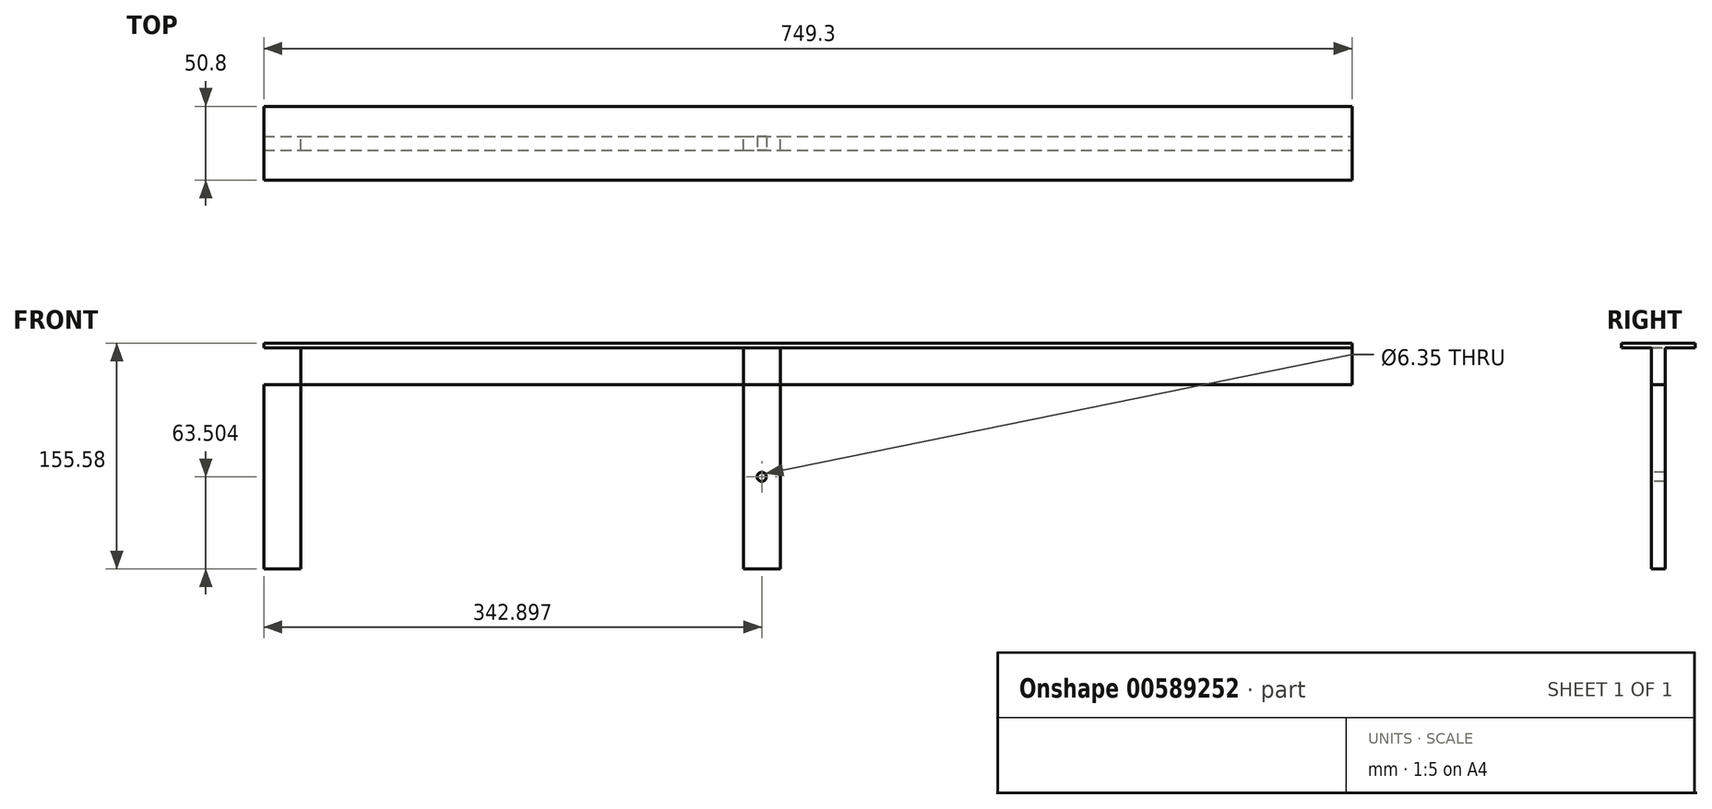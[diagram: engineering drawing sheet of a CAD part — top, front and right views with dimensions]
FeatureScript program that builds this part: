
annotation { "Feature Type Name" : "Feature", "Feature Type Description" : "" }
export const myFeature = defineFeature(function(context is Context, id is Id, definition is map)
    precondition{}
    {
        {
            var Q0;
            Q0=qCreatedBy(makeId("Front.planeOp"),FACE);
            var sketch = newSketch(context, id + "F0", { "sketchPlane" : qUnion([Q0])});
            skLineSegment(sketch, "E0.bottom", {"start": v(-685.15, -7.83) * mm, "end": v(64.15, -7.83) * mm});
            skLineSegment(sketch, "E0.top", {"start": v(-685.15, -33.23) * mm, "end": v(64.15, -33.23) * mm});
            skLineSegment(sketch, "E0.left", {"start": v(-685.15, -7.83) * mm, "end": v(-685.15, -33.23) * mm});
            skLineSegment(sketch, "E0.right", {"start": v(64.15, -7.83) * mm, "end": v(64.15, -33.23) * mm});
            skLineSegment(sketch, "E1.bottom", {"start": v(-685.15, -7.83) * mm, "end": v(-659.75, -7.83) * mm});
            skLineSegment(sketch, "E1.top", {"start": v(-685.15, -160.23) * mm, "end": v(-659.75, -160.23) * mm});
            skLineSegment(sketch, "E1.left", {"start": v(-685.15, -7.83) * mm, "end": v(-685.15, -160.23) * mm});
            skLineSegment(sketch, "E1.right", {"start": v(-659.75, -7.83) * mm, "end": v(-659.75, -160.23) * mm});
            skLineSegment(sketch, "E2.bottom", {"start": v(-354.95, -7.83) * mm, "end": v(-329.55, -7.83) * mm});
            skLineSegment(sketch, "E2.top", {"start": v(-354.95, -160.23) * mm, "end": v(-329.55, -160.23) * mm});
            skLineSegment(sketch, "E2.left", {"start": v(-354.95, -7.83) * mm, "end": v(-354.95, -160.23) * mm});
            skLineSegment(sketch, "E2.right", {"start": v(-329.55, -7.83) * mm, "end": v(-329.55, -160.23) * mm});
            skSolve(sketch);
        }
        {
            var Q0;
            {var subQ0=sQuery(id+"F0.wireOp",EDGE,"E0.right");Q0=makeQuery(id+"F0.imprint","IMPRINT",FACE,{"disambiguationData":[TD([[makeQuery(id+"F0.imprint","IMPRINT",EDGE,{"derivedFrom":subQ0}),-1.0]])]});}
            var Q1;
            {var subQ5=sQuery(id+"F0.wireOp",EDGE,"E2.bottom");Q1=makeQuery(id+"F0.imprint","IMPRINT",FACE,{"disambiguationData":[TD([[makeQuery(id+"F0.imprint","IMPRINT",EDGE,{"derivedFrom":subQ5}),-1.0]])]});}
            var Q2;
            {var subQ5=sQuery(id+"F0.wireOp",EDGE,"E2.top");Q2=makeQuery(id+"F0.imprint","IMPRINT",FACE,{"disambiguationData":[TD([[makeQuery(id+"F0.imprint","IMPRINT",EDGE,{"derivedFrom":subQ5}),1.0]])]});}
            var Q3;
            {var subQ0=sQuery(id+"F0.wireOp",EDGE,"E1.right");var subQ5=sQuery(id+"F0.wireOp",EDGE,"E0.top");var subQ7=makeQuery(id+"F0.imprint","INTERSECT",VERTEX,{"derivedFrom":[subQ5,subQ0]});Q3=makeQuery(id+"F0.imprint","IMPRINT",FACE,{"disambiguationData":[TD([[makeQuery(id+"F0.imprint","IMPRINT",EDGE,{"disambiguationData":[TD([[subQ7,-1.0]])],"derivedFrom":subQ5}),1.0]])]});}
            var Q4;
            {var subQ5=sQuery(id+"F0.wireOp",EDGE,"E1.bottom");Q4=makeQuery(id+"F0.imprint","IMPRINT",FACE,{"disambiguationData":[TD([[makeQuery(id+"F0.imprint","IMPRINT",EDGE,{"derivedFrom":subQ5}),-1.0]])]});}
            var Q5;
            {var subQ5=sQuery(id+"F0.wireOp",EDGE,"E1.top");Q5=makeQuery(id+"F0.imprint","IMPRINT",FACE,{"disambiguationData":[TD([[makeQuery(id+"F0.imprint","IMPRINT",EDGE,{"derivedFrom":subQ5}),1.0]])]});}
            extrude(context, id + "F1", {"entities" : qUnion([Q0, Q1, Q2, Q3, Q4, Q5]), "depth" : (3 / 8 * 25.4) * mm, "offsetDistance" : 25 * mm});
        }
        {
            var Q0;
            Q0=makeQuery(id+"F1.opExtrude","SWEPT_FACE",FACE,{"disambiguationData":[OSD([sQuery(id+"F0.wireOp",EDGE,"E0.bottom"),sQuery(id+"F0.wireOp",EDGE,"E1.bottom"),sQuery(id+"F0.wireOp",EDGE,"E2.bottom")])]});
            var sketch = newSketch(context, id + "F2", { "sketchPlane" : qUnion([Q0])});
            skLineSegment(sketch, "E3.bottom", {"start": v(-685.15, 20.64) * mm, "end": v(64.15, 20.64) * mm});
            skLineSegment(sketch, "E3.top", {"start": v(-685.15, -30.16) * mm, "end": v(64.15, -30.16) * mm});
            skLineSegment(sketch, "E3.left", {"start": v(-685.15, 20.64) * mm, "end": v(-685.15, -30.16) * mm});
            skLineSegment(sketch, "E3.right", {"start": v(64.15, 20.64) * mm, "end": v(64.15, -30.16) * mm});
            skLineSegment(sketch, "E4", {"start": v(-631.47, -4.76) * mm, "end": v(-611.32, -4.76) * mm, "construction": true});
            skPoint(sketch, "E4.startSnap0", {"position": v(-685.15, -4.76) * mm});
            skPoint(sketch, "E4.endSnap0", {"position": v(-685.15, -4.76) * mm});
            skSolve(sketch);
        }
        {
            var Q0;
            {var subQ0=sQuery(id+"F2.wireOp",EDGE,"E3.bottom");Q0=makeQuery(id+"F2.imprint","IMPRINT",FACE,{"disambiguationData":[TD([[makeQuery(id+"F2.imprint","IMPRINT",EDGE,{"derivedFrom":subQ0}),-1.0]])]});}
            var Q1;
            {var subQ1=sQuery(id+"F0.wireOp",EDGE,"E2.bottom");var subQ2=sQuery(id+"F0.wireOp",EDGE,"E1.bottom");var subQ3=sQuery(id+"F0.wireOp",EDGE,"E0.bottom");var subQ4=makeQuery(id+"F1.opExtrude","CAP_EDGE",EDGE,{"disambiguationData":[OSD([subQ3,subQ2,subQ1])],"isStart":true});Q1=makeQuery(id+"F2.imprint","IMPRINT",FACE,{"disambiguationData":[TD([[makeQuery(id+"F2.imprint","IMPRINT",EDGE,{"derivedFrom":subQ4}),-1.0]])]});}
            var Q2;
            {var subQ0=sQuery(id+"F2.wireOp",EDGE,"E3.top");Q2=makeQuery(id+"F2.imprint","IMPRINT",FACE,{"disambiguationData":[TD([[makeQuery(id+"F2.imprint","IMPRINT",EDGE,{"derivedFrom":subQ0}),1.0]])]});}
            extrude(context, id + "F3", {"entities" : qUnion([Q0, Q1, Q2]), "operationType" : NewBodyOperationType.ADD, "depth" : (1 / 8 * 25.4) * mm, "offsetDistance" : 25 * mm});
        }
        {
            var Q0;
            Q0=makeQuery(id+"F1.opExtrude","CAP_FACE",FACE,{"disambiguationData":[OSD([sQuery(id+"F0.wireOp",EDGE,"E0.bottom"),sQuery(id+"F0.wireOp",EDGE,"E0.top"),sQuery(id+"F0.wireOp",EDGE,"E0.right"),sQuery(id+"F0.wireOp",EDGE,"E1.bottom"),sQuery(id+"F0.wireOp",EDGE,"E1.top"),sQuery(id+"F0.wireOp",EDGE,"E1.left"),sQuery(id+"F0.wireOp",EDGE,"E1.right"),sQuery(id+"F0.wireOp",EDGE,"E2.bottom"),sQuery(id+"F0.wireOp",EDGE,"E2.top"),sQuery(id+"F0.wireOp",EDGE,"E2.left"),sQuery(id+"F0.wireOp",EDGE,"E2.right")])],"isStart":false});
            var sketch = newSketch(context, id + "F4", { "sketchPlane" : qUnion([Q0])});
            skCircle(sketch, "E5", {"center": v(-342.25, -96.73) * mm, "radius": 3.17 * mm});
            skPoint(sketch, "E5.centerSnap0", {"position": v(-342.25, -160.23) * mm});
            skSolve(sketch);
        }
        {
            var Q0;
            Q0=makeQuery(id+"F4.imprint","IMPRINT",FACE,{"disambiguationData":[TD([[makeQuery(id+"F4.imprint","IMPRINT",EDGE,{"derivedFrom":sQuery(id+"F4.wireOp",EDGE,"E5")}),1.0]])]});
            extrude(context, id + "F5", {"entities" : qUnion([Q0]), "operationType" : NewBodyOperationType.REMOVE, "endBound" : BoundingType.THROUGH_ALL, "oppositeDirection" : true, "depth" : 25 * mm, "offsetDistance" : 25 * mm});
        }
        {
            var Q0;
            Q0=makeQuery(id+"F3.opExtrude","CAP_FACE",FACE,{"disambiguationData":[OSD([sQuery(id+"F2.wireOp",EDGE,"E3.bottom"),sQuery(id+"F2.wireOp",EDGE,"E3.top"),sQuery(id+"F2.wireOp",EDGE,"E3.left"),sQuery(id+"F2.wireOp",EDGE,"E3.right")])],"isStart":false});
            var sketch = newSketch(context, id + "F6", { "sketchPlane" : qUnion([Q0])});
            skLineSegment(sketch, "E6", {"start": v(11.54, -4.76) * mm, "end": v(58.32, -4.76) * mm, "construction": true});
            skPoint(sketch, "E6.startSnap0", {"position": v(64.15, -4.76) * mm});
            skLineSegment(sketch, "E7", {"start": v(40.6, -23.75) * mm, "end": v(40.6, 14.53) * mm, "construction": true});
            skPoint(sketch, "E8", {"position": v(40.6, -4.6) * mm});
            skSolve(sketch);
        }
    });
